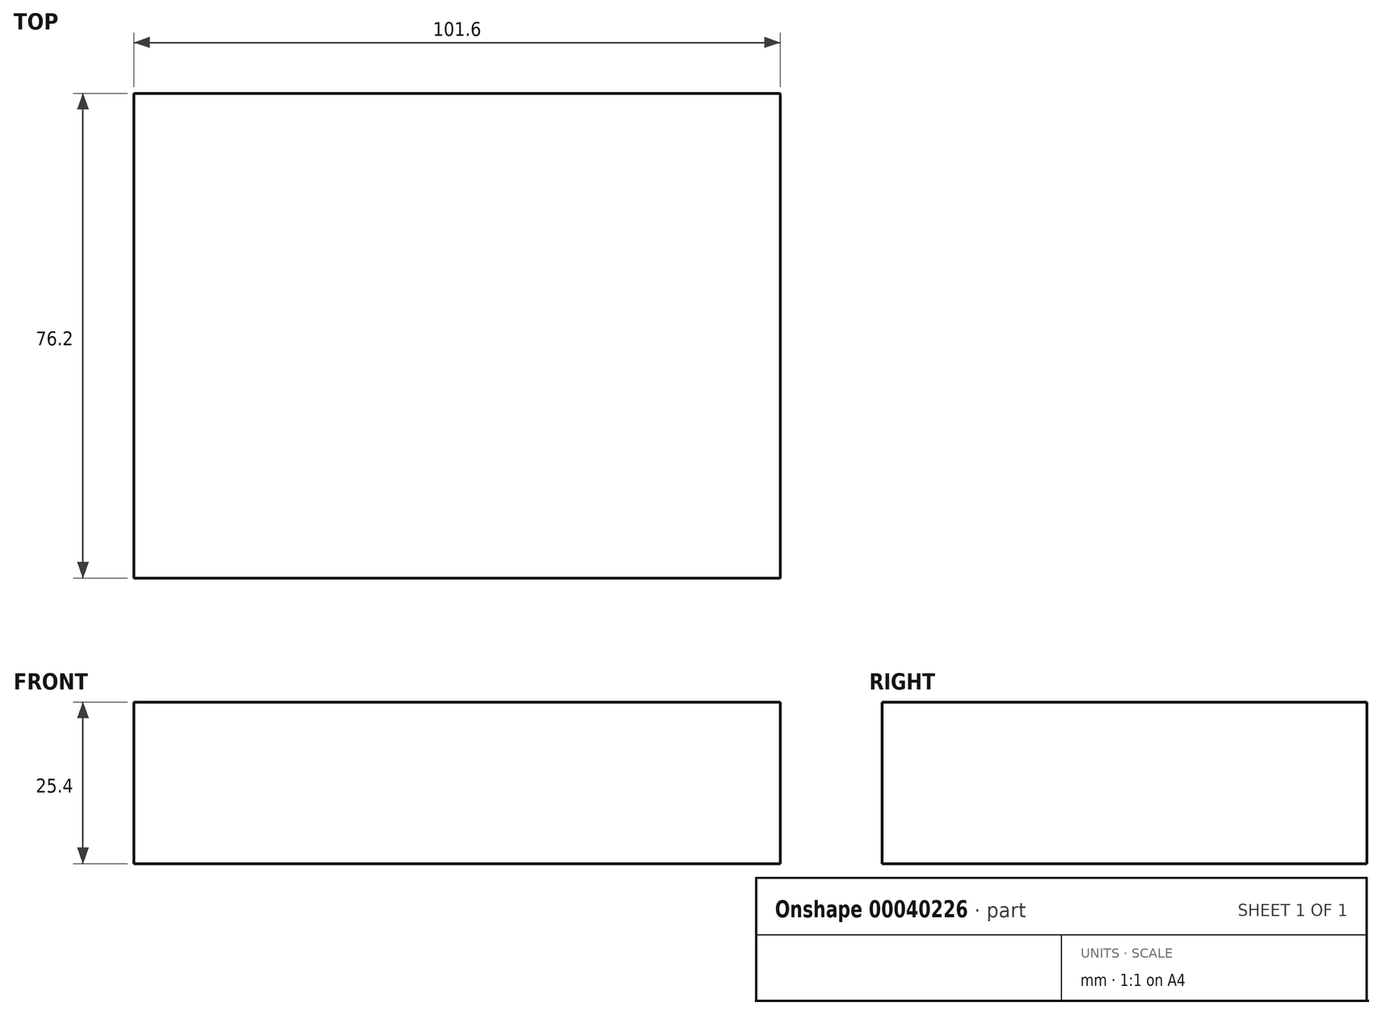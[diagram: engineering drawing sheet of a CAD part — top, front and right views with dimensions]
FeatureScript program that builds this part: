
annotation { "Feature Type Name" : "Feature", "Feature Type Description" : "" }
export const myFeature = defineFeature(function(context is Context, id is Id, definition is map)
    precondition{}
    {
        {
            var Q0;
            Q0=qCreatedBy(makeId("Top.planeOp"),FACE);
            var sketch = newSketch(context, id + "F0", { "sketchPlane" : qUnion([Q0])});
            skLineSegment(sketch, "E0.bottom", {"start": v(-95.83, -25.4) * mm, "end": v(133.77, -25.4) * mm});
            skLineSegment(sketch, "E0.top", {"start": v(-95.83, -144.45) * mm, "end": v(133.77, -144.45) * mm});
            skLineSegment(sketch, "E0.left", {"start": v(-95.83, -25.4) * mm, "end": v(-95.83, -144.45) * mm});
            skLineSegment(sketch, "E0.right", {"start": v(133.77, -25.4) * mm, "end": v(133.77, -144.45) * mm});
            skLineSegment(sketch, "E1.bottom", {"start": v(22.6, 213.04) * mm, "end": v(171.43, 213.04) * mm});
            skLineSegment(sketch, "E1.top", {"start": v(22.6, 50.8) * mm, "end": v(171.43, 50.8) * mm});
            skLineSegment(sketch, "E1.left", {"start": v(22.6, 213.04) * mm, "end": v(22.6, 50.8) * mm});
            skLineSegment(sketch, "E1.right", {"start": v(171.43, 213.04) * mm, "end": v(171.43, 50.8) * mm});
            skLineSegment(sketch, "E2.bottom", {"start": v(-104.4, 101.6) * mm, "end": v(-2.8, 101.6) * mm});
            skLineSegment(sketch, "E2.top", {"start": v(-104.4, 25.4) * mm, "end": v(-2.8, 25.4) * mm});
            skLineSegment(sketch, "E2.left", {"start": v(-104.4, 101.6) * mm, "end": v(-104.4, 25.4) * mm});
            skLineSegment(sketch, "E2.right", {"start": v(-2.8, 101.6) * mm, "end": v(-2.8, 25.4) * mm});
            skSolve(sketch);
        }
        {
            var Q0;
            Q0=makeQuery(id+"F0.imprint","IMPRINT",FACE,{"disambiguationData":[TD([[makeQuery(id+"F0.imprint","IMPRINT",EDGE,{"derivedFrom":sQuery(id+"F0.wireOp",EDGE,"E2.bottom")}),-1.0]])]});
            extrude(context, id + "F1", {"entities" : qUnion([Q0]), "depth" : 25.4 * mm});
        }
    });
